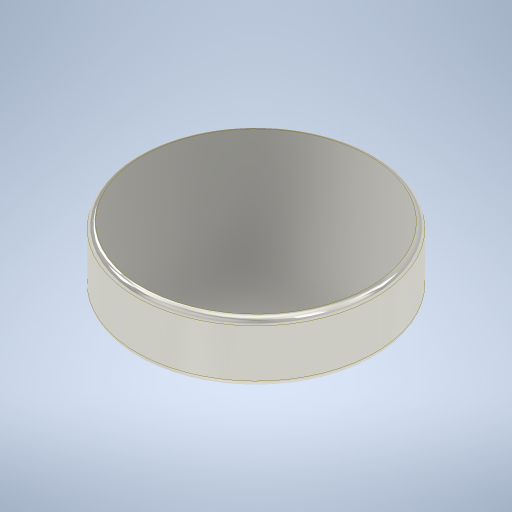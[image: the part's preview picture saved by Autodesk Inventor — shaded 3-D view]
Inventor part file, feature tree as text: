
AUTODESK INVENTOR PART (.ipt)
format: ipt  version: 2023 (Build 270158000, 158)  size: 250,368 bytes
history: native  units: in
note: dims shown in document units (in); Inventor stores cm internally (conversion verified against a paired STEP export)
features: extrude x1, fillet x1, sketch x1
ambient origin geometry x8: Origin, YZ Plane, XZ Plane, XY Plane, X Axis, Y Axis, Z Axis, Center Point
bodies: Solid1 (feature_tree)
feature tree (3):
  extrude  "Extrusion1"  Depth=0.1in TaperAngle=0.0deg
  fillet  "Fillet1"  Radius=0.01in
  sketch  "Sketch1"  dims[d0=0.4in d1=0.1in d2=0.0in d3=0.01in]
